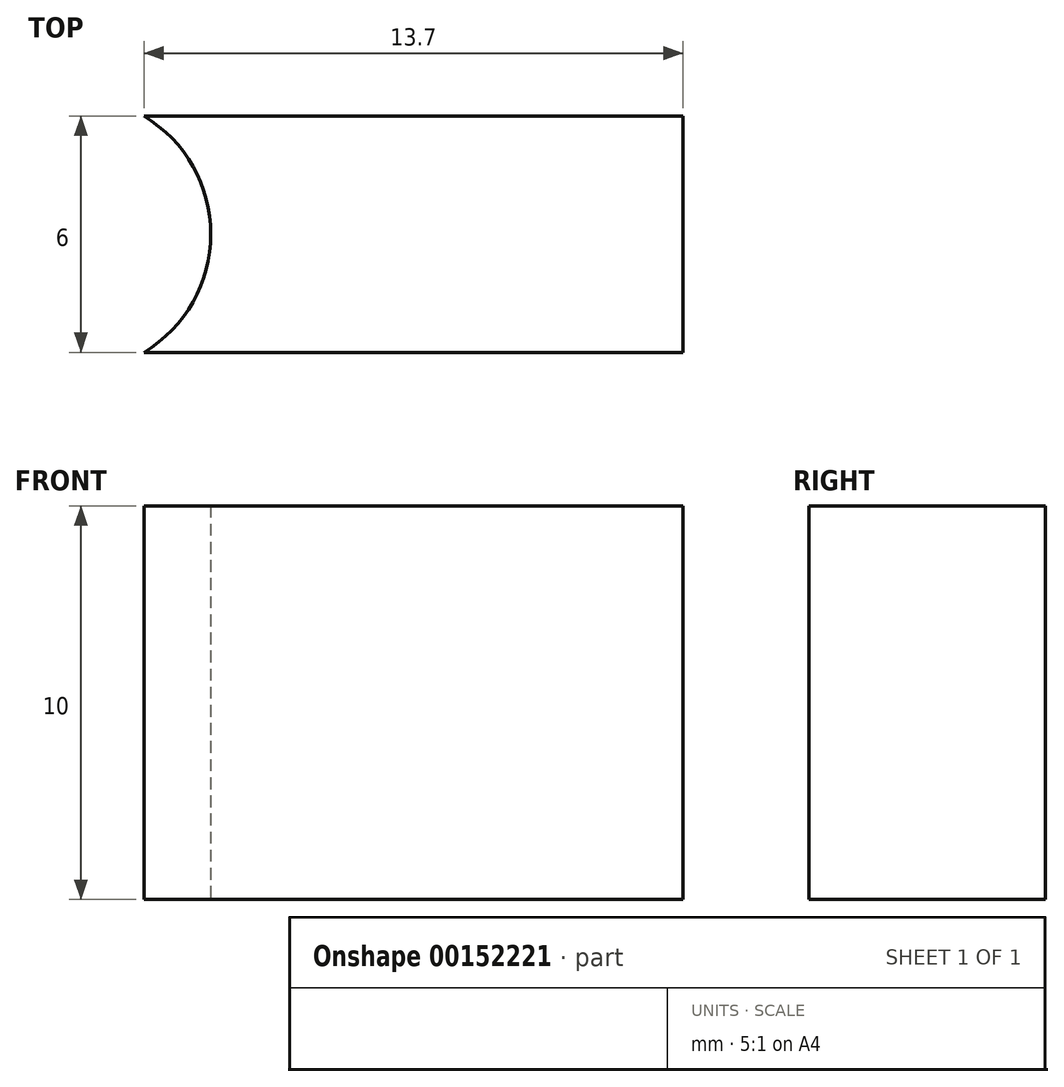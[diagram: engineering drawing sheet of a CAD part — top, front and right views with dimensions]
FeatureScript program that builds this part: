
annotation { "Feature Type Name" : "Feature", "Feature Type Description" : "" }
export const myFeature = defineFeature(function(context is Context, id is Id, definition is map)
    precondition{}
    {
        {
            var Q0;
            Q0=qCreatedBy(makeId("Top.planeOp"),FACE);
            var sketch = newSketch(context, id + "F0", { "sketchPlane" : qUnion([Q0])});
            skLineSegment(sketch, "E0", {"start": v(0, 0) * mm, "end": v(-12, 0) * mm});
            skLineSegment(sketch, "E1", {"start": v(0, 0) * mm, "end": v(0, -6) * mm});
            skLineSegment(sketch, "E2", {"start": v(0, -6) * mm, "end": v(-12, -6) * mm});
            skLineSegment(sketch, "E3", {"start": v(-12, -6) * mm, "end": v(-12, 0) * mm});
            skLineSegment(sketch, "E4", {"start": v(-12, -3) * mm, "end": v(-15.5, -3) * mm});
            skCircle(sketch, "E5", {"center": v(-15.5, -3) * mm, "radius": 3.5 * mm});
            skLineSegment(sketch, "E6", {"start": v(-12, 0) * mm, "end": v(-14.26, 0) * mm});
            skLineSegment(sketch, "E7", {"start": v(-12, -6) * mm, "end": v(-15.2, -6) * mm});
            skSolve(sketch);
        }
        {
            var Q0;
            {var subQ3=sQuery(id+"F0.wireOp",EDGE,"E0");Q0=makeQuery(id+"F0.imprint","IMPRINT",FACE,{"disambiguationData":[TD([[makeQuery(id+"F0.imprint","IMPRINT",EDGE,{"derivedFrom":subQ3}),1.0]])]});}
            var Q1;
            {var subQ1=sQuery(id+"F0.wireOp",EDGE,"E3");var subQ3=sQuery(id+"F0.wireOp",EDGE,"E5");var subQ4=makeQuery(id+"F0.imprint","INTERSECT",VERTEX,{"derivedFrom":[subQ1,subQ3]});Q1=makeQuery(id+"F0.imprint","IMPRINT",FACE,{"disambiguationData":[TD([[makeQuery(id+"F0.imprint","IMPRINT",EDGE,{"disambiguationData":[TD([[subQ4,1.0]])],"derivedFrom":subQ3}),-1.0]])]});}
            var Q2;
            {var subQ1=sQuery(id+"F0.wireOp",EDGE,"E3");var subQ3=sQuery(id+"F0.wireOp",EDGE,"E5");var subQ4=makeQuery(id+"F0.imprint","INTERSECT",VERTEX,{"derivedFrom":[subQ1,subQ3]});Q2=makeQuery(id+"F0.imprint","IMPRINT",FACE,{"disambiguationData":[TD([[makeQuery(id+"F0.imprint","IMPRINT",EDGE,{"disambiguationData":[TD([[subQ4,-1.0]])],"derivedFrom":subQ3}),-1.0]])]});}
            extrude(context, id + "F1", {"entities" : qUnion([Q0, Q1, Q2]), "depth" : 10 * mm});
        }
    });
